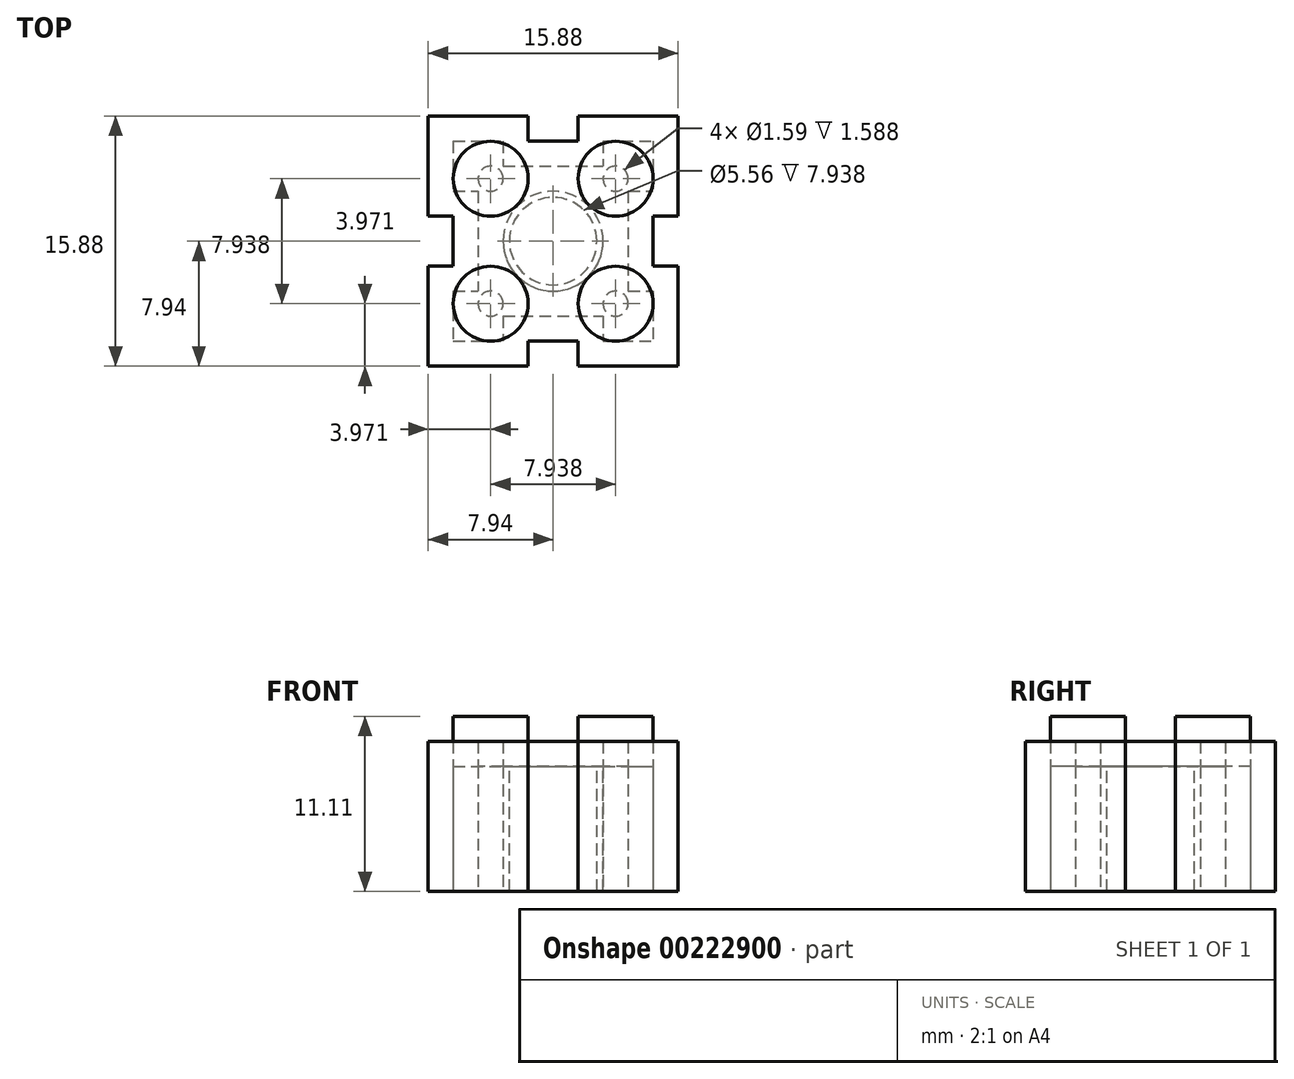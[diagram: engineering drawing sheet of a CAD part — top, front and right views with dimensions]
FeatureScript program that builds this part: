
annotation { "Feature Type Name" : "Feature", "Feature Type Description" : "" }
export const myFeature = defineFeature(function(context is Context, id is Id, definition is map)
    precondition{}
    {
        {
            var Q0;
            Q0=qCreatedBy(makeId("Top.planeOp"),FACE);
            var sketch = newSketch(context, id + "F0", { "sketchPlane" : qUnion([Q0])});
            skLineSegment(sketch, "E0.bottom", {"start": v(-7.94, 7.94) * mm, "end": v(7.94, 7.94) * mm});
            skLineSegment(sketch, "E0.top", {"start": v(-7.94, -7.94) * mm, "end": v(7.94, -7.94) * mm});
            skLineSegment(sketch, "E0.left", {"start": v(-7.94, 7.94) * mm, "end": v(-7.94, -7.94) * mm});
            skLineSegment(sketch, "E0.right", {"start": v(7.94, 7.94) * mm, "end": v(7.94, -7.94) * mm});
            skPoint(sketch, "E0.middle", {"position": v(0, 0) * mm});
            skLineSegment(sketch, "E1.bottom", {"start": v(-6.35, 6.35) * mm, "end": v(6.35, 6.35) * mm});
            skLineSegment(sketch, "E1.top", {"start": v(-6.35, -6.35) * mm, "end": v(6.35, -6.35) * mm});
            skLineSegment(sketch, "E1.left", {"start": v(-6.35, 6.35) * mm, "end": v(-6.35, -6.35) * mm});
            skLineSegment(sketch, "E1.right", {"start": v(6.35, 6.35) * mm, "end": v(6.35, -6.35) * mm});
            skLineSegment(sketch, "E2.bottom", {"start": v(-7.94, 1.59) * mm, "end": v(7.94, 1.59) * mm});
            skLineSegment(sketch, "E2.top", {"start": v(-7.94, -1.59) * mm, "end": v(7.94, -1.59) * mm});
            skLineSegment(sketch, "E2.left", {"start": v(-7.94, 1.59) * mm, "end": v(-7.94, -1.59) * mm});
            skLineSegment(sketch, "E2.right", {"start": v(7.94, 1.59) * mm, "end": v(7.94, -1.59) * mm});
            skLineSegment(sketch, "E3.bottom", {"start": v(-1.59, 7.94) * mm, "end": v(1.59, 7.94) * mm});
            skLineSegment(sketch, "E3.top", {"start": v(-1.59, -7.94) * mm, "end": v(1.59, -7.94) * mm});
            skLineSegment(sketch, "E3.left", {"start": v(-1.59, 7.94) * mm, "end": v(-1.59, -7.94) * mm});
            skLineSegment(sketch, "E3.right", {"start": v(1.59, 7.94) * mm, "end": v(1.59, -7.94) * mm});
            skLineSegment(sketch, "E4", {"start": v(-6.35, 6.35) * mm, "end": v(-1.59, 1.59) * mm});
            skLineSegment(sketch, "E5", {"start": v(1.59, 1.59) * mm, "end": v(6.35, 6.35) * mm});
            skLineSegment(sketch, "E6", {"start": v(1.59, -1.59) * mm, "end": v(6.35, -6.35) * mm});
            skLineSegment(sketch, "E7", {"start": v(-6.35, -6.35) * mm, "end": v(-1.59, -1.59) * mm});
            skCircle(sketch, "E8", {"center": v(-3.97, 3.97) * mm, "radius": 2.38 * mm});
            skCircle(sketch, "E9", {"center": v(3.97, 3.97) * mm, "radius": 2.38 * mm});
            skCircle(sketch, "E10", {"center": v(-3.97, -3.97) * mm, "radius": 2.38 * mm});
            skCircle(sketch, "E11", {"center": v(3.97, -3.97) * mm, "radius": 2.38 * mm});
            skSolve(sketch);
        }
        {
            var Q0;
            {var subQ0=sQuery(id+"F0.wireOp",EDGE,"E8");var subQ1=sQuery(id+"F0.wireOp",EDGE,"E1.bottom");var subQ2=makeQuery(id+"F0.imprint","INTERSECT",VERTEX,{"derivedFrom":[subQ1,subQ0]});Q0=makeQuery(id+"F0.imprint","IMPRINT",FACE,{"disambiguationData":[TD([[makeQuery(id+"F0.imprint","IMPRINT",EDGE,{"disambiguationData":[TD([[subQ2,-1.0]])],"derivedFrom":subQ1}),1.0]])]});}
            var Q1;
            {var subQ1=sQuery(id+"F0.wireOp",EDGE,"E1.bottom");var subQ3=sQuery(id+"F0.wireOp",EDGE,"E8");var subQ4=makeQuery(id+"F0.imprint","INTERSECT",VERTEX,{"derivedFrom":[subQ1,subQ3]});Q1=makeQuery(id+"F0.imprint","IMPRINT",FACE,{"disambiguationData":[TD([[makeQuery(id+"F0.imprint","IMPRINT",EDGE,{"disambiguationData":[TD([[subQ4,-1.0]])],"derivedFrom":subQ3}),-1.0]])]});}
            var Q2;
            {var subQ1=sQuery(id+"F0.wireOp",EDGE,"E1.left");var subQ3=sQuery(id+"F0.wireOp",EDGE,"E8");var subQ4=makeQuery(id+"F0.imprint","INTERSECT",VERTEX,{"derivedFrom":[subQ1,subQ3]});Q2=makeQuery(id+"F0.imprint","IMPRINT",FACE,{"disambiguationData":[TD([[makeQuery(id+"F0.imprint","IMPRINT",EDGE,{"disambiguationData":[TD([[subQ4,1.0]])],"derivedFrom":subQ3}),-1.0]])]});}
            var Q3;
            {var subQ5=sQuery(id+"F0.wireOp",EDGE,"E3.bottom");Q3=makeQuery(id+"F0.imprint","IMPRINT",FACE,{"disambiguationData":[TD([[makeQuery(id+"F0.imprint","IMPRINT",EDGE,{"derivedFrom":subQ5}),-1.0]])]});}
            var Q4;
            {var subQ0=sQuery(id+"F0.wireOp",EDGE,"E3.left");var subQ6=sQuery(id+"F0.wireOp",EDGE,"E1.bottom");var subQ7=makeQuery(id+"F0.imprint","INTERSECT",VERTEX,{"derivedFrom":[subQ6,subQ0]});Q4=makeQuery(id+"F0.imprint","IMPRINT",FACE,{"disambiguationData":[TD([[makeQuery(id+"F0.imprint","IMPRINT",EDGE,{"disambiguationData":[TD([[subQ7,-1.0]])],"derivedFrom":subQ6}),-1.0]])]});}
            var Q5;
            {var subQ1=sQuery(id+"F0.wireOp",EDGE,"E1.bottom");var subQ5=sQuery(id+"F0.wireOp",EDGE,"E3.right");var subQ6=makeQuery(id+"F0.imprint","INTERSECT",VERTEX,{"derivedFrom":[subQ1,subQ5]});Q5=makeQuery(id+"F0.imprint","IMPRINT",FACE,{"disambiguationData":[TD([[makeQuery(id+"F0.imprint","IMPRINT",EDGE,{"disambiguationData":[TD([[subQ6,-1.0]])],"derivedFrom":subQ1}),1.0]])]});}
            var Q6;
            {var subQ0=sQuery(id+"F0.wireOp",EDGE,"E3.right");var subQ1=sQuery(id+"F0.wireOp",EDGE,"E1.bottom");var subQ2=makeQuery(id+"F0.imprint","INTERSECT",VERTEX,{"derivedFrom":[subQ1,subQ0]});Q6=makeQuery(id+"F0.imprint","IMPRINT",FACE,{"disambiguationData":[TD([[makeQuery(id+"F0.imprint","IMPRINT",EDGE,{"disambiguationData":[TD([[subQ2,-1.0]])],"derivedFrom":subQ1}),-1.0]])]});}
            var Q7;
            {var subQ5=sQuery(id+"F0.wireOp",EDGE,"E3.bottom");Q7=makeQuery(id+"F0.imprint","IMPRINT",FACE,{"disambiguationData":[TD([[makeQuery(id+"F0.imprint","IMPRINT",EDGE,{"derivedFrom":subQ5}),-1.0]])]});}
            var Q8;
            {var subQ1=sQuery(id+"F0.wireOp",EDGE,"E1.right");var subQ3=sQuery(id+"F0.wireOp",EDGE,"E9");var subQ4=makeQuery(id+"F0.imprint","INTERSECT",VERTEX,{"derivedFrom":[subQ1,subQ3]});Q8=makeQuery(id+"F0.imprint","IMPRINT",FACE,{"disambiguationData":[TD([[makeQuery(id+"F0.imprint","IMPRINT",EDGE,{"disambiguationData":[TD([[subQ4,-1.0]])],"derivedFrom":subQ3}),-1.0]])]});}
            var Q9;
            {var subQ1=sQuery(id+"F0.wireOp",EDGE,"E1.bottom");var subQ3=sQuery(id+"F0.wireOp",EDGE,"E9");var subQ4=makeQuery(id+"F0.imprint","INTERSECT",VERTEX,{"derivedFrom":[subQ1,subQ3]});Q9=makeQuery(id+"F0.imprint","IMPRINT",FACE,{"disambiguationData":[TD([[makeQuery(id+"F0.imprint","IMPRINT",EDGE,{"disambiguationData":[TD([[subQ4,1.0]])],"derivedFrom":subQ3}),-1.0]])]});}
            var Q10;
            {var subQ0=sQuery(id+"F0.wireOp",EDGE,"E9");var subQ1=sQuery(id+"F0.wireOp",EDGE,"E1.right");var subQ2=makeQuery(id+"F0.imprint","INTERSECT",VERTEX,{"derivedFrom":[subQ1,subQ0]});Q10=makeQuery(id+"F0.imprint","IMPRINT",FACE,{"disambiguationData":[TD([[makeQuery(id+"F0.imprint","IMPRINT",EDGE,{"disambiguationData":[TD([[subQ2,-1.0]])],"derivedFrom":subQ1}),-1.0]])]});}
            var Q11;
            {var subQ1=sQuery(id+"F0.wireOp",EDGE,"E2.bottom");var subQ3=sQuery(id+"F0.wireOp",EDGE,"E9");var subQ4=makeQuery(id+"F0.imprint","INTERSECT",VERTEX,{"derivedFrom":[subQ1,subQ3]});Q11=makeQuery(id+"F0.imprint","IMPRINT",FACE,{"disambiguationData":[TD([[makeQuery(id+"F0.imprint","IMPRINT",EDGE,{"disambiguationData":[TD([[subQ4,1.0]])],"derivedFrom":subQ3}),-1.0]])]});}
            var Q12;
            {var subQ1=sQuery(id+"F0.wireOp",EDGE,"E3.right");var subQ3=sQuery(id+"F0.wireOp",EDGE,"E9");var subQ4=makeQuery(id+"F0.imprint","INTERSECT",VERTEX,{"derivedFrom":[subQ1,subQ3]});Q12=makeQuery(id+"F0.imprint","IMPRINT",FACE,{"disambiguationData":[TD([[makeQuery(id+"F0.imprint","IMPRINT",EDGE,{"disambiguationData":[TD([[subQ4,-1.0]])],"derivedFrom":subQ3}),-1.0]])]});}
            var Q13;
            {var subQ0=sQuery(id+"F0.wireOp",EDGE,"E8");var subQ1=sQuery(id+"F0.wireOp",EDGE,"E1.bottom");var subQ2=makeQuery(id+"F0.imprint","INTERSECT",VERTEX,{"derivedFrom":[subQ1,subQ0]});Q13=makeQuery(id+"F0.imprint","IMPRINT",FACE,{"disambiguationData":[TD([[makeQuery(id+"F0.imprint","IMPRINT",EDGE,{"disambiguationData":[TD([[subQ2,-1.0]])],"derivedFrom":subQ1}),-1.0]])]});}
            var Q14;
            {var subQ1=sQuery(id+"F0.wireOp",EDGE,"E3.left");var subQ3=sQuery(id+"F0.wireOp",EDGE,"E8");var subQ4=makeQuery(id+"F0.imprint","INTERSECT",VERTEX,{"derivedFrom":[subQ1,subQ3]});Q14=makeQuery(id+"F0.imprint","IMPRINT",FACE,{"disambiguationData":[TD([[makeQuery(id+"F0.imprint","IMPRINT",EDGE,{"disambiguationData":[TD([[subQ4,1.0]])],"derivedFrom":subQ3}),-1.0]])]});}
            var Q15;
            {var subQ1=sQuery(id+"F0.wireOp",EDGE,"E2.bottom");var subQ3=sQuery(id+"F0.wireOp",EDGE,"E8");var subQ4=makeQuery(id+"F0.imprint","INTERSECT",VERTEX,{"derivedFrom":[subQ1,subQ3]});Q15=makeQuery(id+"F0.imprint","IMPRINT",FACE,{"disambiguationData":[TD([[makeQuery(id+"F0.imprint","IMPRINT",EDGE,{"disambiguationData":[TD([[subQ4,-1.0]])],"derivedFrom":subQ3}),-1.0]])]});}
            var Q16;
            {var subQ0=sQuery(id+"F0.wireOp",EDGE,"E8");var subQ1=sQuery(id+"F0.wireOp",EDGE,"E1.left");var subQ2=makeQuery(id+"F0.imprint","INTERSECT",VERTEX,{"derivedFrom":[subQ1,subQ0]});Q16=makeQuery(id+"F0.imprint","IMPRINT",FACE,{"disambiguationData":[TD([[makeQuery(id+"F0.imprint","IMPRINT",EDGE,{"disambiguationData":[TD([[subQ2,-1.0]])],"derivedFrom":subQ1}),1.0]])]});}
            var Q17;
            {var subQ5=sQuery(id+"F0.wireOp",EDGE,"E2.left");Q17=makeQuery(id+"F0.imprint","IMPRINT",FACE,{"disambiguationData":[TD([[makeQuery(id+"F0.imprint","IMPRINT",EDGE,{"derivedFrom":subQ5}),1.0]])]});}
            var Q18;
            {var subQ1=sQuery(id+"F0.wireOp",EDGE,"E2.bottom");var subQ4=sQuery(id+"F0.wireOp",EDGE,"E1.left");var subQ5=makeQuery(id+"F0.imprint","INTERSECT",VERTEX,{"derivedFrom":[subQ4,subQ1]});Q18=makeQuery(id+"F0.imprint","IMPRINT",FACE,{"disambiguationData":[TD([[makeQuery(id+"F0.imprint","IMPRINT",EDGE,{"disambiguationData":[TD([[subQ5,-1.0]])],"derivedFrom":subQ4}),1.0]])]});}
            var Q19;
            {var subQ0=sQuery(id+"F0.wireOp",EDGE,"E3.left");var subQ1=sQuery(id+"F0.wireOp",EDGE,"E2.bottom");var subQ2=makeQuery(id+"F0.imprint","INTERSECT",VERTEX,{"derivedFrom":[subQ1,subQ0,sQuery(id+"F0.wireOp",EDGE,"E4")]});Q19=makeQuery(id+"F0.imprint","IMPRINT",FACE,{"disambiguationData":[TD([[makeQuery(id+"F0.imprint","IMPRINT",EDGE,{"disambiguationData":[TD([[subQ2,-1.0]])],"derivedFrom":subQ1}),-1.0]])]});}
            var Q20;
            {var subQ4=sQuery(id+"F0.wireOp",EDGE,"E2.bottom");var subQ5=sQuery(id+"F0.wireOp",EDGE,"E1.right");var subQ6=makeQuery(id+"F0.imprint","INTERSECT",VERTEX,{"derivedFrom":[subQ5,subQ4]});Q20=makeQuery(id+"F0.imprint","IMPRINT",FACE,{"disambiguationData":[TD([[makeQuery(id+"F0.imprint","IMPRINT",EDGE,{"disambiguationData":[TD([[subQ6,-1.0]])],"derivedFrom":subQ5}),-1.0]])]});}
            var Q21;
            {var subQ5=sQuery(id+"F0.wireOp",EDGE,"E2.right");Q21=makeQuery(id+"F0.imprint","IMPRINT",FACE,{"disambiguationData":[TD([[makeQuery(id+"F0.imprint","IMPRINT",EDGE,{"derivedFrom":subQ5}),-1.0]])]});}
            var Q22;
            {var subQ0=sQuery(id+"F0.wireOp",EDGE,"E3.left");var subQ1=sQuery(id+"F0.wireOp",EDGE,"E1.top");var subQ2=makeQuery(id+"F0.imprint","INTERSECT",VERTEX,{"derivedFrom":[subQ1,subQ0]});Q22=makeQuery(id+"F0.imprint","IMPRINT",FACE,{"disambiguationData":[TD([[makeQuery(id+"F0.imprint","IMPRINT",EDGE,{"disambiguationData":[TD([[subQ2,-1.0]])],"derivedFrom":subQ1}),1.0]])]});}
            var Q23;
            {var subQ1=sQuery(id+"F0.wireOp",EDGE,"E3.right");var subQ3=sQuery(id+"F0.wireOp",EDGE,"E11");var subQ4=makeQuery(id+"F0.imprint","INTERSECT",VERTEX,{"derivedFrom":[subQ1,subQ3]});Q23=makeQuery(id+"F0.imprint","IMPRINT",FACE,{"disambiguationData":[TD([[makeQuery(id+"F0.imprint","IMPRINT",EDGE,{"disambiguationData":[TD([[subQ4,1.0]])],"derivedFrom":subQ3}),-1.0]])]});}
            var Q24;
            {var subQ1=sQuery(id+"F0.wireOp",EDGE,"E2.top");var subQ3=sQuery(id+"F0.wireOp",EDGE,"E11");var subQ4=makeQuery(id+"F0.imprint","INTERSECT",VERTEX,{"derivedFrom":[subQ1,subQ3]});Q24=makeQuery(id+"F0.imprint","IMPRINT",FACE,{"disambiguationData":[TD([[makeQuery(id+"F0.imprint","IMPRINT",EDGE,{"disambiguationData":[TD([[subQ4,-1.0]])],"derivedFrom":subQ3}),-1.0]])]});}
            var Q25;
            {var subQ0=sQuery(id+"F0.wireOp",EDGE,"E2.top");var subQ1=sQuery(id+"F0.wireOp",EDGE,"E1.right");var subQ2=makeQuery(id+"F0.imprint","INTERSECT",VERTEX,{"derivedFrom":[subQ1,subQ0]});Q25=makeQuery(id+"F0.imprint","IMPRINT",FACE,{"disambiguationData":[TD([[makeQuery(id+"F0.imprint","IMPRINT",EDGE,{"disambiguationData":[TD([[subQ2,-1.0]])],"derivedFrom":subQ1}),-1.0]])]});}
            var Q26;
            {var subQ1=sQuery(id+"F0.wireOp",EDGE,"E1.right");var subQ3=sQuery(id+"F0.wireOp",EDGE,"E11");var subQ4=makeQuery(id+"F0.imprint","INTERSECT",VERTEX,{"derivedFrom":[subQ1,subQ3]});Q26=makeQuery(id+"F0.imprint","IMPRINT",FACE,{"disambiguationData":[TD([[makeQuery(id+"F0.imprint","IMPRINT",EDGE,{"disambiguationData":[TD([[subQ4,1.0]])],"derivedFrom":subQ3}),-1.0]])]});}
            var Q27;
            {var subQ1=sQuery(id+"F0.wireOp",EDGE,"E1.top");var subQ3=sQuery(id+"F0.wireOp",EDGE,"E11");var subQ4=makeQuery(id+"F0.imprint","INTERSECT",VERTEX,{"derivedFrom":[subQ1,subQ3]});Q27=makeQuery(id+"F0.imprint","IMPRINT",FACE,{"disambiguationData":[TD([[makeQuery(id+"F0.imprint","IMPRINT",EDGE,{"disambiguationData":[TD([[subQ4,-1.0]])],"derivedFrom":subQ3}),-1.0]])]});}
            var Q28;
            {var subQ0=sQuery(id+"F0.wireOp",EDGE,"E3.right");var subQ1=sQuery(id+"F0.wireOp",EDGE,"E1.top");var subQ2=makeQuery(id+"F0.imprint","INTERSECT",VERTEX,{"derivedFrom":[subQ1,subQ0]});Q28=makeQuery(id+"F0.imprint","IMPRINT",FACE,{"disambiguationData":[TD([[makeQuery(id+"F0.imprint","IMPRINT",EDGE,{"disambiguationData":[TD([[subQ2,-1.0]])],"derivedFrom":subQ1}),1.0]])]});}
            var Q29;
            {var subQ6=sQuery(id+"F0.wireOp",EDGE,"E1.top");var subQ10=sQuery(id+"F0.wireOp",EDGE,"E3.right");var subQ11=makeQuery(id+"F0.imprint","INTERSECT",VERTEX,{"derivedFrom":[subQ6,subQ10]});Q29=makeQuery(id+"F0.imprint","IMPRINT",FACE,{"disambiguationData":[TD([[makeQuery(id+"F0.imprint","IMPRINT",EDGE,{"disambiguationData":[TD([[subQ11,-1.0]])],"derivedFrom":subQ6}),-1.0]])]});}
            var Q30;
            {var subQ5=sQuery(id+"F0.wireOp",EDGE,"E3.top");Q30=makeQuery(id+"F0.imprint","IMPRINT",FACE,{"disambiguationData":[TD([[makeQuery(id+"F0.imprint","IMPRINT",EDGE,{"derivedFrom":subQ5}),1.0]])]});}
            var Q31;
            {var subQ0=sQuery(id+"F0.wireOp",EDGE,"E10");var subQ1=sQuery(id+"F0.wireOp",EDGE,"E1.top");var subQ2=makeQuery(id+"F0.imprint","INTERSECT",VERTEX,{"derivedFrom":[subQ1,subQ0]});Q31=makeQuery(id+"F0.imprint","IMPRINT",FACE,{"disambiguationData":[TD([[makeQuery(id+"F0.imprint","IMPRINT",EDGE,{"disambiguationData":[TD([[subQ2,-1.0]])],"derivedFrom":subQ1}),-1.0]])]});}
            var Q32;
            {var subQ1=sQuery(id+"F0.wireOp",EDGE,"E1.top");var subQ3=sQuery(id+"F0.wireOp",EDGE,"E10");var subQ4=makeQuery(id+"F0.imprint","INTERSECT",VERTEX,{"derivedFrom":[subQ1,subQ3]});Q32=makeQuery(id+"F0.imprint","IMPRINT",FACE,{"disambiguationData":[TD([[makeQuery(id+"F0.imprint","IMPRINT",EDGE,{"disambiguationData":[TD([[subQ4,1.0]])],"derivedFrom":subQ3}),-1.0]])]});}
            var Q33;
            {var subQ1=sQuery(id+"F0.wireOp",EDGE,"E1.left");var subQ3=sQuery(id+"F0.wireOp",EDGE,"E10");var subQ4=makeQuery(id+"F0.imprint","INTERSECT",VERTEX,{"derivedFrom":[subQ1,subQ3]});Q33=makeQuery(id+"F0.imprint","IMPRINT",FACE,{"disambiguationData":[TD([[makeQuery(id+"F0.imprint","IMPRINT",EDGE,{"disambiguationData":[TD([[subQ4,-1.0]])],"derivedFrom":subQ3}),-1.0]])]});}
            var Q34;
            {var subQ0=sQuery(id+"F0.wireOp",EDGE,"E2.top");var subQ1=sQuery(id+"F0.wireOp",EDGE,"E1.left");var subQ2=makeQuery(id+"F0.imprint","INTERSECT",VERTEX,{"derivedFrom":[subQ1,subQ0]});Q34=makeQuery(id+"F0.imprint","IMPRINT",FACE,{"disambiguationData":[TD([[makeQuery(id+"F0.imprint","IMPRINT",EDGE,{"disambiguationData":[TD([[subQ2,-1.0]])],"derivedFrom":subQ1}),1.0]])]});}
            var Q35;
            {var subQ1=sQuery(id+"F0.wireOp",EDGE,"E2.top");var subQ3=sQuery(id+"F0.wireOp",EDGE,"E10");var subQ4=makeQuery(id+"F0.imprint","INTERSECT",VERTEX,{"derivedFrom":[subQ1,subQ3]});Q35=makeQuery(id+"F0.imprint","IMPRINT",FACE,{"disambiguationData":[TD([[makeQuery(id+"F0.imprint","IMPRINT",EDGE,{"disambiguationData":[TD([[subQ4,1.0]])],"derivedFrom":subQ3}),-1.0]])]});}
            var Q36;
            {var subQ1=sQuery(id+"F0.wireOp",EDGE,"E3.left");var subQ3=sQuery(id+"F0.wireOp",EDGE,"E10");var subQ4=makeQuery(id+"F0.imprint","INTERSECT",VERTEX,{"derivedFrom":[subQ1,subQ3]});Q36=makeQuery(id+"F0.imprint","IMPRINT",FACE,{"disambiguationData":[TD([[makeQuery(id+"F0.imprint","IMPRINT",EDGE,{"disambiguationData":[TD([[subQ4,-1.0]])],"derivedFrom":subQ3}),-1.0]])]});}
            var Q37;
            {var subQ0=sQuery(id+"F0.wireOp",EDGE,"E10");var subQ1=sQuery(id+"F0.wireOp",EDGE,"E1.top");var subQ2=makeQuery(id+"F0.imprint","INTERSECT",VERTEX,{"derivedFrom":[subQ1,subQ0]});Q37=makeQuery(id+"F0.imprint","IMPRINT",FACE,{"disambiguationData":[TD([[makeQuery(id+"F0.imprint","IMPRINT",EDGE,{"disambiguationData":[TD([[subQ2,-1.0]])],"derivedFrom":subQ1}),1.0]])]});}
            extrude(context, id + "F1", {"entities" : qUnion([Q0, Q1, Q2, Q3, Q4, Q5, Q6, Q7, Q8, Q9, Q10, Q11, Q12, Q13, Q14, Q15, Q16, Q17, Q18, Q19, Q20, Q21, Q22, Q23, Q24, Q25, Q26, Q27, Q28, Q29, Q30, Q31, Q32, Q33, Q34, Q35, Q36, Q37]), "depth" : 9.52 * mm});
        }
        {
            var Q0;
            {var subQ0=sQuery(id+"F0.wireOp",EDGE,"E8");var subQ1=sQuery(id+"F0.wireOp",EDGE,"E4");var subQ2=makeQuery(id+"F0.imprint","INTERSECT",VERTEX,{"disambiguationData":[OD(0.0)],"derivedFrom":[subQ1,subQ0]});Q0=makeQuery(id+"F0.imprint","IMPRINT",FACE,{"disambiguationData":[TD([[makeQuery(id+"F0.imprint","IMPRINT",EDGE,{"disambiguationData":[TD([[subQ2,-1.0]])],"derivedFrom":subQ1}),-1.0]])]});}
            var Q1;
            {var subQ0=sQuery(id+"F0.wireOp",EDGE,"E8");var subQ1=sQuery(id+"F0.wireOp",EDGE,"E4");var subQ2=makeQuery(id+"F0.imprint","INTERSECT",VERTEX,{"disambiguationData":[OD(0.0)],"derivedFrom":[subQ1,subQ0]});Q1=makeQuery(id+"F0.imprint","IMPRINT",FACE,{"disambiguationData":[TD([[makeQuery(id+"F0.imprint","IMPRINT",EDGE,{"disambiguationData":[TD([[subQ2,-1.0]])],"derivedFrom":subQ1}),1.0]])]});}
            var Q2;
            {var subQ0=sQuery(id+"F0.wireOp",EDGE,"E9");var subQ1=sQuery(id+"F0.wireOp",EDGE,"E5");var subQ2=makeQuery(id+"F0.imprint","INTERSECT",VERTEX,{"disambiguationData":[OD(0.0)],"derivedFrom":[subQ1,subQ0]});Q2=makeQuery(id+"F0.imprint","IMPRINT",FACE,{"disambiguationData":[TD([[makeQuery(id+"F0.imprint","IMPRINT",EDGE,{"disambiguationData":[TD([[subQ2,-1.0]])],"derivedFrom":subQ1}),1.0]])]});}
            var Q3;
            {var subQ0=sQuery(id+"F0.wireOp",EDGE,"E9");var subQ1=sQuery(id+"F0.wireOp",EDGE,"E5");var subQ2=makeQuery(id+"F0.imprint","INTERSECT",VERTEX,{"disambiguationData":[OD(0.0)],"derivedFrom":[subQ1,subQ0]});Q3=makeQuery(id+"F0.imprint","IMPRINT",FACE,{"disambiguationData":[TD([[makeQuery(id+"F0.imprint","IMPRINT",EDGE,{"disambiguationData":[TD([[subQ2,-1.0]])],"derivedFrom":subQ1}),-1.0]])]});}
            var Q4;
            {var subQ0=sQuery(id+"F0.wireOp",EDGE,"E11");var subQ1=sQuery(id+"F0.wireOp",EDGE,"E6");var subQ2=makeQuery(id+"F0.imprint","INTERSECT",VERTEX,{"disambiguationData":[OD(0.0)],"derivedFrom":[subQ1,subQ0]});Q4=makeQuery(id+"F0.imprint","IMPRINT",FACE,{"disambiguationData":[TD([[makeQuery(id+"F0.imprint","IMPRINT",EDGE,{"disambiguationData":[TD([[subQ2,-1.0]])],"derivedFrom":subQ1}),1.0]])]});}
            var Q5;
            {var subQ0=sQuery(id+"F0.wireOp",EDGE,"E11");var subQ1=sQuery(id+"F0.wireOp",EDGE,"E6");var subQ2=makeQuery(id+"F0.imprint","INTERSECT",VERTEX,{"disambiguationData":[OD(0.0)],"derivedFrom":[subQ1,subQ0]});Q5=makeQuery(id+"F0.imprint","IMPRINT",FACE,{"disambiguationData":[TD([[makeQuery(id+"F0.imprint","IMPRINT",EDGE,{"disambiguationData":[TD([[subQ2,-1.0]])],"derivedFrom":subQ1}),-1.0]])]});}
            var Q6;
            {var subQ0=sQuery(id+"F0.wireOp",EDGE,"E10");var subQ1=sQuery(id+"F0.wireOp",EDGE,"E7");var subQ2=makeQuery(id+"F0.imprint","INTERSECT",VERTEX,{"disambiguationData":[OD(0.0)],"derivedFrom":[subQ1,subQ0]});Q6=makeQuery(id+"F0.imprint","IMPRINT",FACE,{"disambiguationData":[TD([[makeQuery(id+"F0.imprint","IMPRINT",EDGE,{"disambiguationData":[TD([[subQ2,-1.0]])],"derivedFrom":subQ1}),-1.0]])]});}
            var Q7;
            {var subQ0=sQuery(id+"F0.wireOp",EDGE,"E10");var subQ1=sQuery(id+"F0.wireOp",EDGE,"E7");var subQ2=makeQuery(id+"F0.imprint","INTERSECT",VERTEX,{"disambiguationData":[OD(0.0)],"derivedFrom":[subQ1,subQ0]});Q7=makeQuery(id+"F0.imprint","IMPRINT",FACE,{"disambiguationData":[TD([[makeQuery(id+"F0.imprint","IMPRINT",EDGE,{"disambiguationData":[TD([[subQ2,-1.0]])],"derivedFrom":subQ1}),1.0]])]});}
            extrude(context, id + "F2", {"entities" : qUnion([Q0, Q1, Q2, Q3, Q4, Q5, Q6, Q7]), "operationType" : NewBodyOperationType.ADD, "depth" : 11.1 * mm});
        }
        {
            var Q0;
            {var subQ0=sQuery(id+"F0.wireOp",EDGE,"E11");var subQ1=sQuery(id+"F0.wireOp",EDGE,"E10");var subQ2=sQuery(id+"F0.wireOp",EDGE,"E9");var subQ3=sQuery(id+"F0.wireOp",EDGE,"E8");Q0=makeQuery(id+"F2.boolean.opBoolean","MERGE",FACE,{"derivedFrom":[makeQuery(id+"F1.opExtrude","CAP_FACE",FACE,{"disambiguationData":[OSD([sQuery(id+"F0.wireOp",EDGE,"E0.bottom"),sQuery(id+"F0.wireOp",EDGE,"E0.top"),sQuery(id+"F0.wireOp",EDGE,"E0.left"),sQuery(id+"F0.wireOp",EDGE,"E0.right"),sQuery(id+"F0.wireOp",EDGE,"E2.left"),sQuery(id+"F0.wireOp",EDGE,"E2.right"),sQuery(id+"F0.wireOp",EDGE,"E3.bottom"),sQuery(id+"F0.wireOp",EDGE,"E3.top"),subQ3,subQ2,subQ1,subQ0])],"isStart":true}),makeQuery(id+"F2.opExtrude","CAP_FACE",FACE,{"disambiguationData":[OSD([subQ3])],"isStart":true}),makeQuery(id+"F2.opExtrude","CAP_FACE",FACE,{"disambiguationData":[OSD([subQ2])],"isStart":true}),makeQuery(id+"F2.opExtrude","CAP_FACE",FACE,{"disambiguationData":[OSD([subQ1])],"isStart":true}),makeQuery(id+"F2.opExtrude","CAP_FACE",FACE,{"disambiguationData":[OSD([subQ0])],"isStart":true})]});}
            shell(context, id + "F3", {"entities" : qUnion([Q0]), "thickness" : 1.59 * mm});
        }
        {
            var Q0;
            Q0=makeQuery(id+"F3.opShell","OFFSET_FACE",FACE,{"disambiguationData":[OSD([sQuery(id+"F0.wireOp",EDGE,"E0.bottom"),sQuery(id+"F0.wireOp",EDGE,"E0.top"),sQuery(id+"F0.wireOp",EDGE,"E0.left"),sQuery(id+"F0.wireOp",EDGE,"E0.right"),sQuery(id+"F0.wireOp",EDGE,"E2.left"),sQuery(id+"F0.wireOp",EDGE,"E2.right"),sQuery(id+"F0.wireOp",EDGE,"E3.bottom"),sQuery(id+"F0.wireOp",EDGE,"E3.top"),sQuery(id+"F0.wireOp",EDGE,"E8"),sQuery(id+"F0.wireOp",EDGE,"E9"),sQuery(id+"F0.wireOp",EDGE,"E10"),sQuery(id+"F0.wireOp",EDGE,"E11")])]});
            var sketch = newSketch(context, id + "F4", { "sketchPlane" : qUnion([Q0])});
            skCircle(sketch, "E12", {"center": v(0, 0) * mm, "radius": 3.18 * mm});
            skCircle(sketch, "E13", {"center": v(0, 0) * mm, "radius": 2.78 * mm});
            skSolve(sketch);
        }
        {
            var Q0;
            Q0=makeQuery(id+"F4.imprint","IMPRINT",FACE,{"disambiguationData":[TD([[makeQuery(id+"F4.imprint","IMPRINT",EDGE,{"derivedFrom":sQuery(id+"F4.wireOp",EDGE,"E12")}),1.0]])]});
            extrude(context, id + "F5", {"entities" : qUnion([Q0]), "operationType" : NewBodyOperationType.ADD, "depth" : 7.94 * mm});
        }
    });
